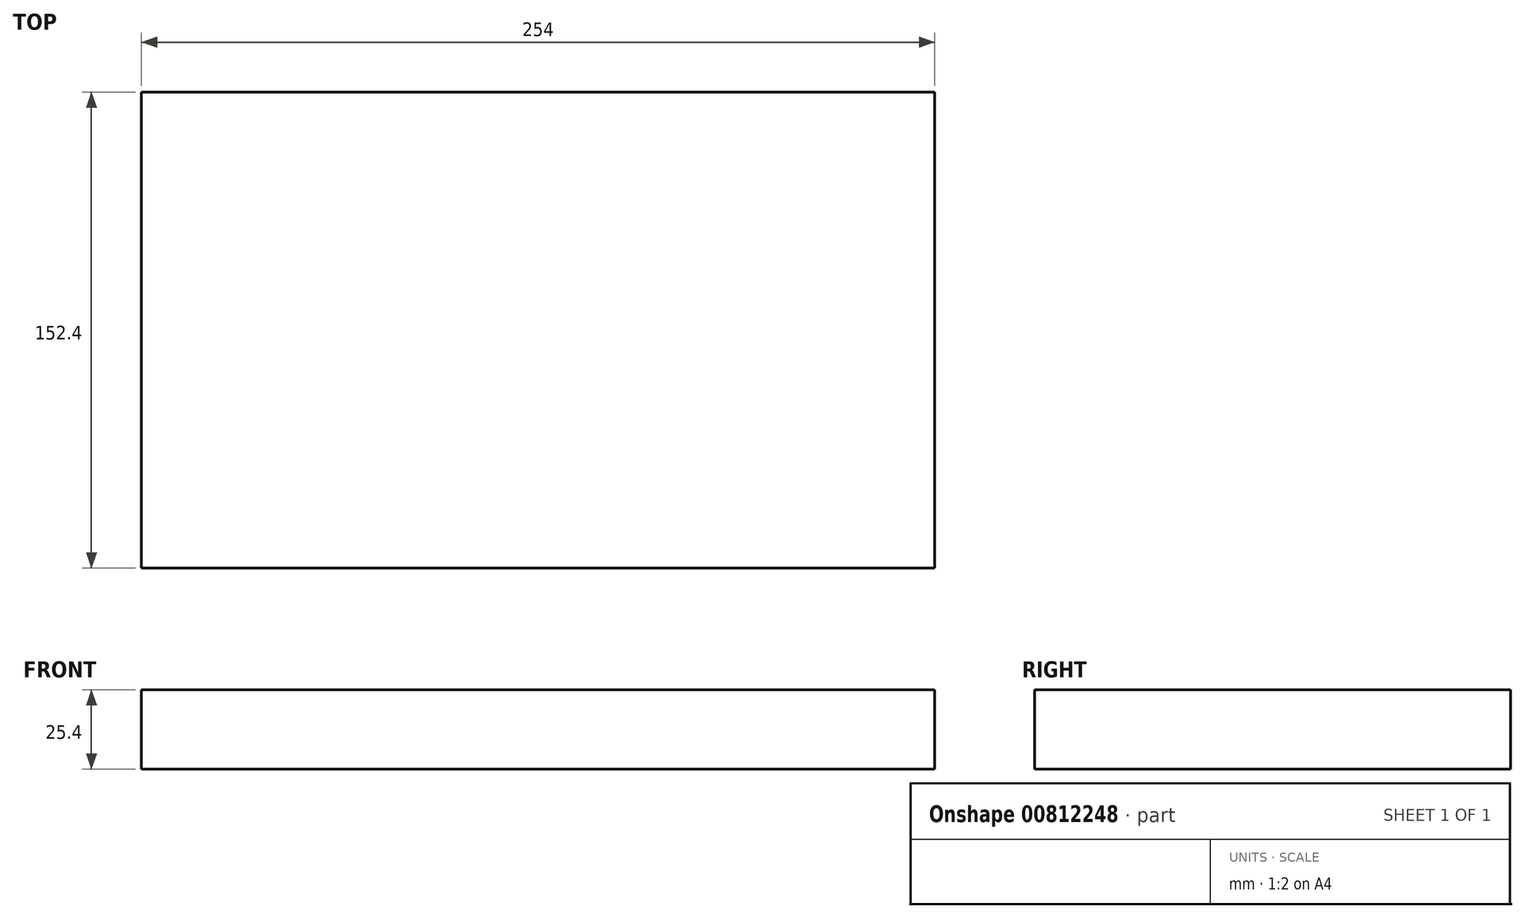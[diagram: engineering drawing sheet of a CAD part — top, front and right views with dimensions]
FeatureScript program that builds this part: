
annotation { "Feature Type Name" : "Feature", "Feature Type Description" : "" }
export const myFeature = defineFeature(function(context is Context, id is Id, definition is map)
    precondition{}
    {
        {
            var Q0;
            Q0=qCreatedBy(makeId("Top.planeOp"),FACE);
            var sketch = newSketch(context, id + "F0", { "sketchPlane" : qUnion([Q0])});
            skLineSegment(sketch, "E0.bottom", {"start": v(127, -76.2) * mm, "end": v(-127, -76.2) * mm});
            skLineSegment(sketch, "E0.top", {"start": v(127, 76.2) * mm, "end": v(-127, 76.2) * mm});
            skLineSegment(sketch, "E0.left", {"start": v(127, -76.2) * mm, "end": v(127, 76.2) * mm});
            skLineSegment(sketch, "E0.right", {"start": v(-127, -76.2) * mm, "end": v(-127, 76.2) * mm});
            skPoint(sketch, "E0.middle", {"position": v(0, 0) * mm});
            skSolve(sketch);
        }
        {
            var Q0;
            Q0 = qSketchRegion(id + "F0", true);
            extrude(context, id + "F1", {"entities" : qUnion([Q0]), "depth" : 25.4 * mm, "offsetDistance" : 25.4 * mm});
        }
    });
